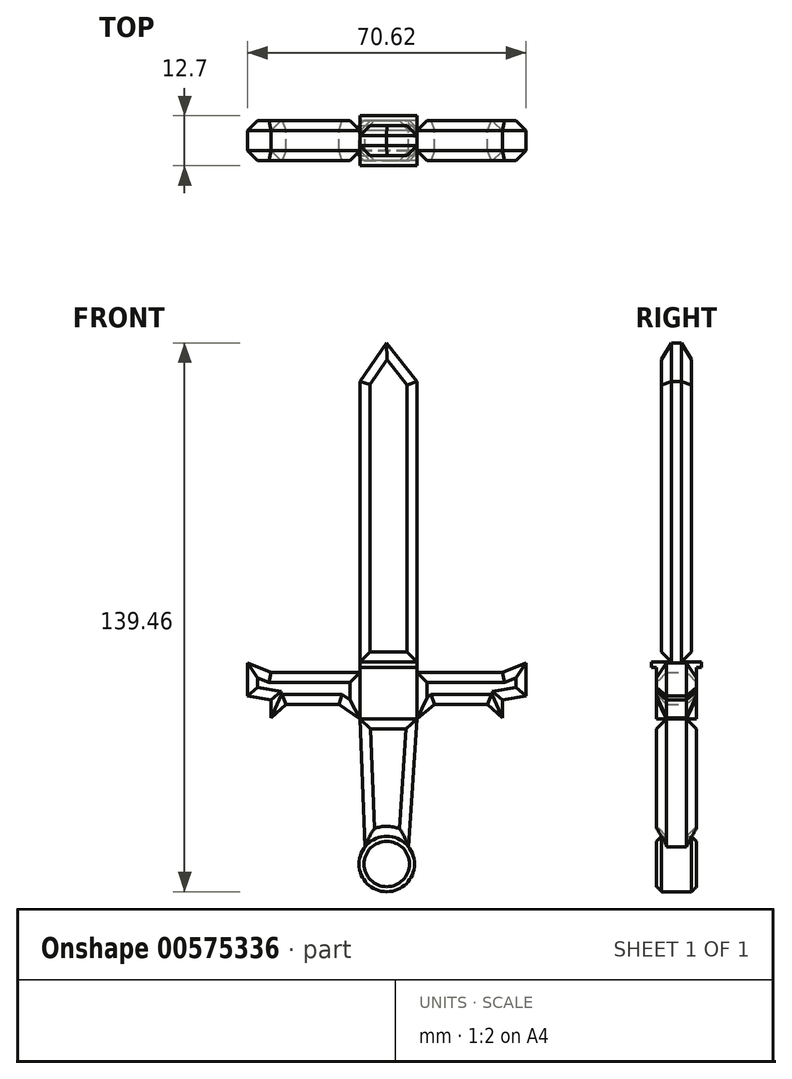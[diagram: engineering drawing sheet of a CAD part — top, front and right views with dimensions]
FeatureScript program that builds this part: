
annotation { "Feature Type Name" : "Feature", "Feature Type Description" : "" }
export const myFeature = defineFeature(function(context is Context, id is Id, definition is map)
    precondition{}
    {
        {
            var Q0;
            Q0=qCreatedBy(makeId("Front.planeOp"),FACE);
            var sketch = newSketch(context, id + "F0", { "sketchPlane" : qUnion([Q0])});
            skLineSegment(sketch, "E0", {"start": v(7.63, -11.8) * mm, "end": v(-6.76, -11.8) * mm});
            skLineSegment(sketch, "E1", {"start": v(-6.76, 0) * mm, "end": v(-6.76, 73.97) * mm});
            skLineSegment(sketch, "E2", {"start": v(-6.76, 73.97) * mm, "end": v(0, 83.76) * mm});
            skLineSegment(sketch, "E3", {"start": v(0, 83.76) * mm, "end": v(7.63, 73.97) * mm});
            skLineSegment(sketch, "E4", {"start": v(7.63, 73.97) * mm, "end": v(7.63, 0) * mm});
            skCircle(sketch, "E5", {"center": v(0, -5.38) * mm, "radius": 6.42 * mm});
            skCircle(sketch, "E6", {"center": v(0, -48.66) * mm, "radius": 7.03 * mm});
            skLineSegment(sketch, "E7", {"start": v(0, -41.63) * mm, "end": v(0, -55.7) * mm});
            skLineSegment(sketch, "E8", {"start": v(7.63, -11.8) * mm, "end": v(5.5, -44.29) * mm});
            skLineSegment(sketch, "E9", {"start": v(-6.76, -11.8) * mm, "end": v(-5.5, -44.29) * mm});
            skLineSegment(sketch, "E10", {"start": v(-6.76, 0) * mm, "end": v(-29.4, 0) * mm});
            skLineSegment(sketch, "E11", {"start": v(-29.4, 0) * mm, "end": v(-35.31, 2.48) * mm});
            skLineSegment(sketch, "E12", {"start": v(-35.31, 2.48) * mm, "end": v(-35.31, -5.9) * mm});
            skLineSegment(sketch, "E13", {"start": v(-35.31, -5.9) * mm, "end": v(-29.4, -6.9) * mm});
            skLineSegment(sketch, "E14", {"start": v(-29.4, -6.9) * mm, "end": v(-29.4, -11.54) * mm});
            skLineSegment(sketch, "E15", {"start": v(-29.4, -11.54) * mm, "end": v(-25.65, -8.1) * mm});
            skLineSegment(sketch, "E16", {"start": v(-25.65, -8.1) * mm, "end": v(-12.18, -8.1) * mm});
            skLineSegment(sketch, "E17", {"start": v(-12.18, -8.1) * mm, "end": v(-6.76, -11.8) * mm});
            skLineSegment(sketch, "E18.MirrorCS", {"start": v(25.65, -8.1) * mm, "end": v(12.18, -8.1) * mm});
            skLineSegment(sketch, "E19.MirrorCS", {"start": v(29.4, -11.54) * mm, "end": v(25.65, -8.1) * mm});
            skLineSegment(sketch, "E20.MirrorCS", {"start": v(29.4, 0) * mm, "end": v(35.31, 2.48) * mm});
            skLineSegment(sketch, "E21.MirrorCS", {"start": v(35.31, 2.48) * mm, "end": v(35.31, -5.9) * mm});
            skLineSegment(sketch, "E22.MirrorCS", {"start": v(35.31, -5.9) * mm, "end": v(29.4, -6.9) * mm});
            skLineSegment(sketch, "E23.MirrorCS", {"start": v(29.4, -6.9) * mm, "end": v(29.4, -11.54) * mm});
            skLineSegment(sketch, "E24", {"start": v(7.63, 0) * mm, "end": v(29.4, 0) * mm});
            skLineSegment(sketch, "E25", {"start": v(-6.76, 1.27) * mm, "end": v(7.63, 1.27) * mm});
            skLineSegment(sketch, "E26", {"start": v(-6.76, 0) * mm, "end": v(-6.76, -11.8) * mm});
            skLineSegment(sketch, "E27", {"start": v(7.63, 0) * mm, "end": v(7.63, -11.8) * mm});
            skLineSegment(sketch, "E28", {"start": v(7.63, -11.8) * mm, "end": v(12.18, -8.1) * mm});
            skLineSegment(sketch, "E29", {"start": v(-6.76, 2.74) * mm, "end": v(7.63, 2.74) * mm});
            skSolve(sketch);
        }
        {
            var Q0;
            {var subQ2=sQuery(id+"F0.wireOp",EDGE,"E8");Q0=makeQuery(id+"F0.imprint","IMPRINT",FACE,{"disambiguationData":[TD([[makeQuery(id+"F0.imprint","IMPRINT",EDGE,{"derivedFrom":subQ2}),-1.0]])]});}
            extrude(context, id + "F1", {"entities" : qUnion([Q0]), "depth" : 5.08 * mm, "offsetDistance" : 25.4 * mm, "hasSecondDirection" : true, "secondDirectionOppositeDirection" : true, "secondDirectionDepth" : 5.08 * mm});
        }
        {
            var Q0;
            Q0=makeQuery(id+"F1.opExtrude","CAP_FACE",FACE,{"disambiguationData":[OSD([sQuery(id+"F0.wireOp",EDGE,"E0"),sQuery(id+"F0.wireOp",EDGE,"E6"),sQuery(id+"F0.wireOp",EDGE,"E8"),sQuery(id+"F0.wireOp",EDGE,"E9")])],"isStart":true});
            var Q1;
            Q1=makeQuery(id+"F1.opExtrude","CAP_FACE",FACE,{"disambiguationData":[OSD([sQuery(id+"F0.wireOp",EDGE,"E0"),sQuery(id+"F0.wireOp",EDGE,"E6"),sQuery(id+"F0.wireOp",EDGE,"E8"),sQuery(id+"F0.wireOp",EDGE,"E9")])],"isStart":false});
            chamfer(context, id + "F2", {"entities" : qUnion([Q0, Q1]), "width" : 2.54 * mm, "tangentPropagation" : true});
        }
        {
            var Q0;
            {var subQ0=sQuery(id+"F0.wireOp",EDGE,"E7");Q0=makeQuery(id+"F0.imprint","IMPRINT",FACE,{"disambiguationData":[TD([[makeQuery(id+"F0.imprint","IMPRINT",EDGE,{"derivedFrom":subQ0}),1.0]])]});}
            var Q1;
            {var subQ0=sQuery(id+"F0.wireOp",EDGE,"E7");Q1=makeQuery(id+"F0.imprint","IMPRINT",FACE,{"disambiguationData":[TD([[makeQuery(id+"F0.imprint","IMPRINT",EDGE,{"derivedFrom":subQ0}),-1.0]])]});}
            extrude(context, id + "F3", {"entities" : qUnion([Q0, Q1]), "operationType" : NewBodyOperationType.ADD, "depth" : 5.08 * mm, "offsetDistance" : 25.4 * mm, "hasSecondDirection" : true, "secondDirectionOppositeDirection" : true, "secondDirectionDepth" : 5.08 * mm});
        }
        {
            var Q0;
            Q0=makeQuery(id+"F3.opExtrude","CAP_FACE",FACE,{"disambiguationData":[OSD([sQuery(id+"F0.wireOp",EDGE,"E6")])],"isStart":true});
            var Q1;
            Q1=makeQuery(id+"F3.opExtrude","CAP_FACE",FACE,{"disambiguationData":[OSD([sQuery(id+"F0.wireOp",EDGE,"E6")])],"isStart":false});
            chamfer(context, id + "F4", {"entities" : qUnion([Q0, Q1]), "width" : 1.27 * mm, "tangentPropagation" : true});
        }
        {
            var Q0;
            Q0=makeQuery(id+"F0.imprint","IMPRINT",FACE,{"disambiguationData":[TD([[makeQuery(id+"F0.imprint","IMPRINT",EDGE,{"derivedFrom":sQuery(id+"F0.wireOp",EDGE,"E18.MirrorCS")}),-1.0]])]});
            var Q1;
            Q1=makeQuery(id+"F0.imprint","IMPRINT",FACE,{"disambiguationData":[TD([[makeQuery(id+"F0.imprint","IMPRINT",EDGE,{"derivedFrom":sQuery(id+"F0.wireOp",EDGE,"E10")}),1.0]])]});
            extrude(context, id + "F5", {"entities" : qUnion([Q0, Q1]), "depth" : 5.08 * mm, "offsetDistance" : 25.4 * mm, "hasSecondDirection" : true, "secondDirectionOppositeDirection" : true, "secondDirectionDepth" : 5.08 * mm});
        }
        {
            var Q0;
            {var subQ6=sQuery(id+"F0.wireOp",EDGE,"E5");Q0=makeQuery(id+"F0.imprint","IMPRINT",FACE,{"disambiguationData":[TD([[makeQuery(id+"F0.imprint","IMPRINT",EDGE,{"derivedFrom":subQ6}),-1.0]])]});}
            var Q1;
            Q1=makeQuery(id+"F0.imprint","IMPRINT",FACE,{"disambiguationData":[TD([[makeQuery(id+"F0.imprint","IMPRINT",EDGE,{"derivedFrom":sQuery(id+"F0.wireOp",EDGE,"E5")}),1.0]])]});
            extrude(context, id + "F6", {"entities" : qUnion([Q0, Q1]), "depth" : 5.08 * mm, "offsetDistance" : 25.4 * mm, "hasSecondDirection" : true, "secondDirectionOppositeDirection" : true, "secondDirectionDepth" : 5.08 * mm});
        }
        {
            var Q0;
            {var subQ3=sQuery(id+"F0.wireOp",EDGE,"E2");Q0=makeQuery(id+"F0.imprint","IMPRINT",FACE,{"disambiguationData":[TD([[makeQuery(id+"F0.imprint","IMPRINT",EDGE,{"derivedFrom":subQ3}),-1.0]])]});}
            extrude(context, id + "F7", {"entities" : qUnion([Q0]), "depth" : 3.8 * mm, "offsetDistance" : 25.4 * mm, "hasSecondDirection" : true, "secondDirectionOppositeDirection" : true, "secondDirectionDepth" : 3.8 * mm});
        }
        {
            var Q0;
            Q0=makeQuery(id+"F5.opExtrude","CAP_FACE",FACE,{"disambiguationData":[OSD([sQuery(id+"F0.wireOp",EDGE,"E10"),sQuery(id+"F0.wireOp",EDGE,"E11"),sQuery(id+"F0.wireOp",EDGE,"E12"),sQuery(id+"F0.wireOp",EDGE,"E13"),sQuery(id+"F0.wireOp",EDGE,"E14"),sQuery(id+"F0.wireOp",EDGE,"E15"),sQuery(id+"F0.wireOp",EDGE,"E16"),sQuery(id+"F0.wireOp",EDGE,"E17"),sQuery(id+"F0.wireOp",EDGE,"E26")])],"isStart":false});
            var Q1;
            Q1=makeQuery(id+"F5.opExtrude","CAP_FACE",FACE,{"disambiguationData":[OSD([sQuery(id+"F0.wireOp",EDGE,"E18.MirrorCS"),sQuery(id+"F0.wireOp",EDGE,"E19.MirrorCS"),sQuery(id+"F0.wireOp",EDGE,"E20.MirrorCS"),sQuery(id+"F0.wireOp",EDGE,"E21.MirrorCS"),sQuery(id+"F0.wireOp",EDGE,"E22.MirrorCS"),sQuery(id+"F0.wireOp",EDGE,"E23.MirrorCS"),sQuery(id+"F0.wireOp",EDGE,"E24"),sQuery(id+"F0.wireOp",EDGE,"E27"),sQuery(id+"F0.wireOp",EDGE,"E28")])],"isStart":false});
            var Q2;
            Q2=makeQuery(id+"F5.opExtrude","CAP_FACE",FACE,{"disambiguationData":[OSD([sQuery(id+"F0.wireOp",EDGE,"E10"),sQuery(id+"F0.wireOp",EDGE,"E11"),sQuery(id+"F0.wireOp",EDGE,"E12"),sQuery(id+"F0.wireOp",EDGE,"E13"),sQuery(id+"F0.wireOp",EDGE,"E14"),sQuery(id+"F0.wireOp",EDGE,"E15"),sQuery(id+"F0.wireOp",EDGE,"E16"),sQuery(id+"F0.wireOp",EDGE,"E17"),sQuery(id+"F0.wireOp",EDGE,"E26")])],"isStart":true});
            var Q3;
            Q3=makeQuery(id+"F5.opExtrude","CAP_FACE",FACE,{"disambiguationData":[OSD([sQuery(id+"F0.wireOp",EDGE,"E18.MirrorCS"),sQuery(id+"F0.wireOp",EDGE,"E19.MirrorCS"),sQuery(id+"F0.wireOp",EDGE,"E20.MirrorCS"),sQuery(id+"F0.wireOp",EDGE,"E21.MirrorCS"),sQuery(id+"F0.wireOp",EDGE,"E22.MirrorCS"),sQuery(id+"F0.wireOp",EDGE,"E23.MirrorCS"),sQuery(id+"F0.wireOp",EDGE,"E24"),sQuery(id+"F0.wireOp",EDGE,"E27"),sQuery(id+"F0.wireOp",EDGE,"E28")])],"isStart":true});
            chamfer(context, id + "F8", {"entities" : qUnion([Q0, Q1, Q2, Q3]), "width" : 2.54 * mm, "tangentPropagation" : true});
        }
        {
            var Q0;
            Q0=makeQuery(id+"F7.opExtrude","CAP_FACE",FACE,{"disambiguationData":[OSD([sQuery(id+"F0.wireOp",EDGE,"E1"),sQuery(id+"F0.wireOp",EDGE,"E2"),sQuery(id+"F0.wireOp",EDGE,"E3"),sQuery(id+"F0.wireOp",EDGE,"E4"),sQuery(id+"F0.wireOp",EDGE,"E29")])],"isStart":true});
            var Q1;
            Q1=makeQuery(id+"F7.opExtrude","CAP_FACE",FACE,{"disambiguationData":[OSD([sQuery(id+"F0.wireOp",EDGE,"E1"),sQuery(id+"F0.wireOp",EDGE,"E2"),sQuery(id+"F0.wireOp",EDGE,"E3"),sQuery(id+"F0.wireOp",EDGE,"E4"),sQuery(id+"F0.wireOp",EDGE,"E29")])],"isStart":false});
            chamfer(context, id + "F9", {"entities" : qUnion([Q0, Q1]), "width" : 2.54 * mm, "tangentPropagation" : true});
        }
        {
            var Q0;
            {var subQ0=sQuery(id+"F0.wireOp",EDGE,"E25");Q0=makeQuery(id+"F0.imprint","IMPRINT",FACE,{"disambiguationData":[TD([[makeQuery(id+"F0.imprint","IMPRINT",EDGE,{"derivedFrom":subQ0}),1.0]])]});}
            extrude(context, id + "F10", {"entities" : qUnion([Q0]), "operationType" : NewBodyOperationType.ADD, "depth" : 6.35 * mm, "offsetDistance" : 25.4 * mm, "hasSecondDirection" : true, "secondDirectionOppositeDirection" : true, "secondDirectionDepth" : 6.35 * mm});
        }
    });
